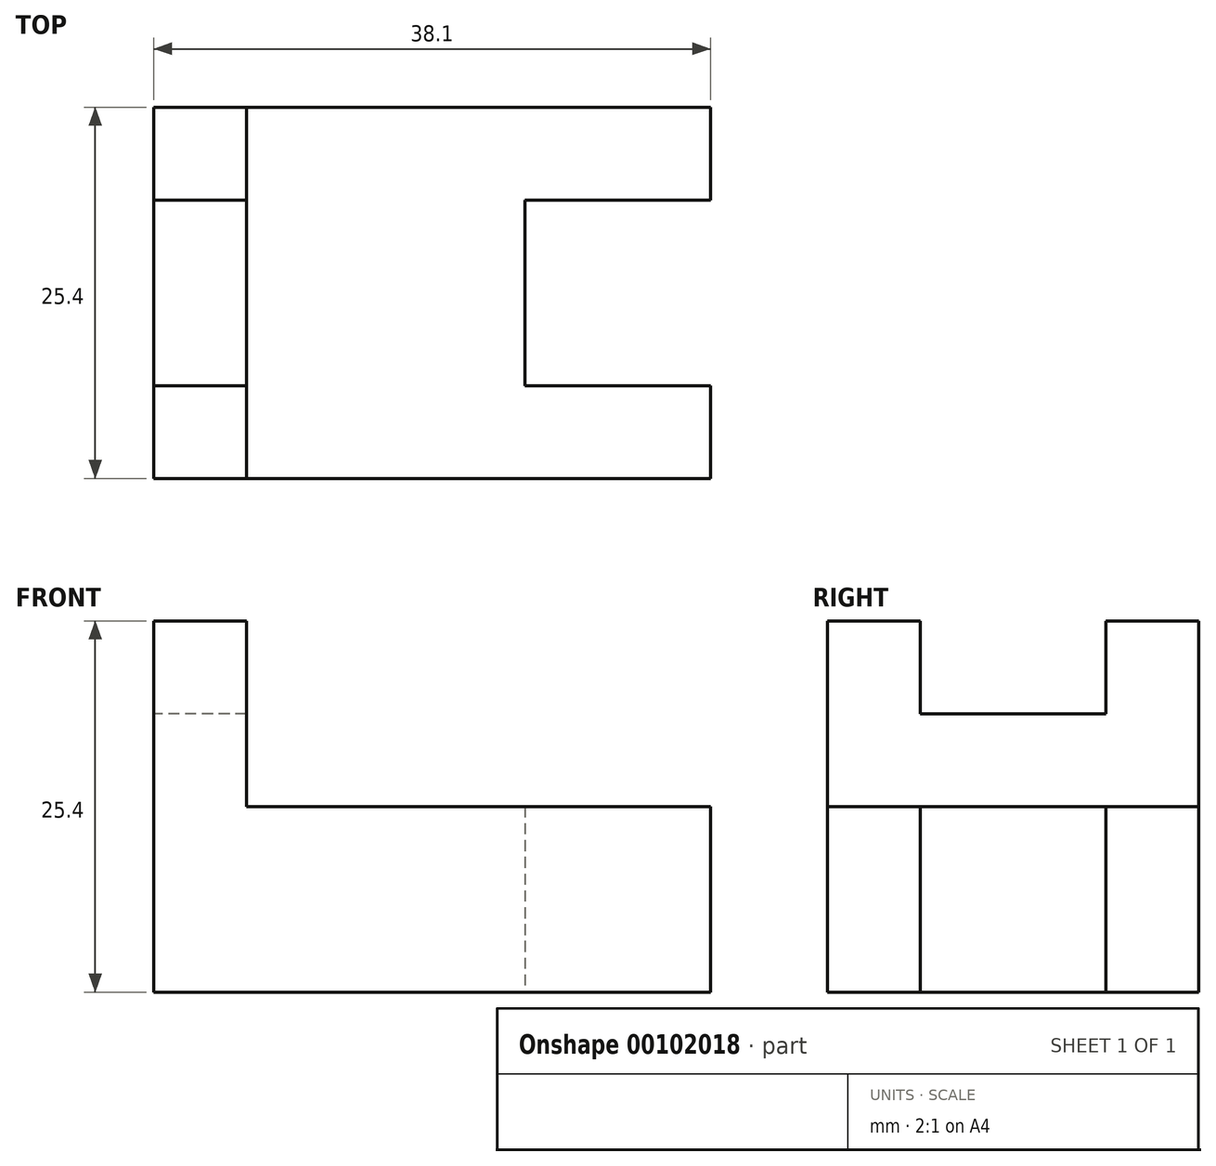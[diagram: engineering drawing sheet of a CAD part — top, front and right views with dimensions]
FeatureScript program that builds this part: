
annotation { "Feature Type Name" : "Feature", "Feature Type Description" : "" }
export const myFeature = defineFeature(function(context is Context, id is Id, definition is map)
    precondition{}
    {
        {
            var Q0;
            Q0=qCreatedBy(makeId("Top.planeOp"),FACE);
            var sketch = newSketch(context, id + "F0", { "sketchPlane" : qUnion([Q0])});
            skLineSegment(sketch, "E0", {"start": v(0, 0) * mm, "end": v(38.1, 0) * mm});
            skLineSegment(sketch, "E1", {"start": v(38.1, 0) * mm, "end": v(38.1, 6.35) * mm});
            skLineSegment(sketch, "E2", {"start": v(38.1, 6.35) * mm, "end": v(25.4, 6.35) * mm});
            skLineSegment(sketch, "E3", {"start": v(25.4, 6.35) * mm, "end": v(25.4, 19.05) * mm});
            skLineSegment(sketch, "E4", {"start": v(25.4, 19.05) * mm, "end": v(38.1, 19.05) * mm});
            skLineSegment(sketch, "E5", {"start": v(38.1, 19.05) * mm, "end": v(38.1, 25.4) * mm});
            skLineSegment(sketch, "E6", {"start": v(38.1, 25.4) * mm, "end": v(0, 25.4) * mm});
            skLineSegment(sketch, "E7", {"start": v(0, 25.4) * mm, "end": v(0, 0) * mm});
            skSolve(sketch);
        }
        {
            var Q0;
            Q0 = qSketchRegion(id + "F0", true);
            extrude(context, id + "F1", {"entities" : qUnion([Q0]), "depth" : 12.7 * mm});
        }
        {
            var Q0;
            Q0=makeQuery(id+"F1.opExtrude","CAP_FACE",FACE,{"disambiguationData":[OSD([sQuery(id+"F0.wireOp",EDGE,"E0"),sQuery(id+"F0.wireOp",EDGE,"E1"),sQuery(id+"F0.wireOp",EDGE,"E2"),sQuery(id+"F0.wireOp",EDGE,"E3"),sQuery(id+"F0.wireOp",EDGE,"E4"),sQuery(id+"F0.wireOp",EDGE,"E5"),sQuery(id+"F0.wireOp",EDGE,"E6"),sQuery(id+"F0.wireOp",EDGE,"E7")])],"isStart":false});
            var sketch = newSketch(context, id + "F2", { "sketchPlane" : qUnion([Q0])});
            skLineSegment(sketch, "E8", {"start": v(0, 0) * mm, "end": v(0, 25.4) * mm});
            skLineSegment(sketch, "E9", {"start": v(0, 25.4) * mm, "end": v(6.35, 25.4) * mm});
            skLineSegment(sketch, "E10", {"start": v(6.35, 25.4) * mm, "end": v(6.35, 0) * mm});
            skLineSegment(sketch, "E11", {"start": v(6.35, 0) * mm, "end": v(0, 0) * mm});
            skSolve(sketch);
        }
        {
            var Q0;
            Q0 = qSketchRegion(id + "F2", true);
            extrude(context, id + "F3", {"entities" : qUnion([Q0]), "operationType" : NewBodyOperationType.ADD, "depth" : 12.7 * mm});
        }
        {
            var Q0;
            Q0=makeQuery(id+"F3.opExtrude","CAP_FACE",FACE,{"disambiguationData":[OSD([sQuery(id+"F2.wireOp",EDGE,"E8"),sQuery(id+"F2.wireOp",EDGE,"E9"),sQuery(id+"F2.wireOp",EDGE,"E10"),sQuery(id+"F2.wireOp",EDGE,"E11")])],"isStart":false});
            var sketch = newSketch(context, id + "F4", { "sketchPlane" : qUnion([Q0])});
            skLineSegment(sketch, "E12.bottom", {"start": v(6.35, 19.05) * mm, "end": v(0, 19.05) * mm});
            skLineSegment(sketch, "E12.top", {"start": v(6.35, 6.35) * mm, "end": v(0, 6.35) * mm});
            skLineSegment(sketch, "E12.left", {"start": v(6.35, 19.05) * mm, "end": v(6.35, 6.35) * mm});
            skLineSegment(sketch, "E12.right", {"start": v(0, 19.05) * mm, "end": v(0, 6.35) * mm});
            skPoint(sketch, "E12.middle", {"position": v(3.17, 12.7) * mm});
            skPoint(sketch, "E12.middle.positionSnap0", {"position": v(3.17, 25.4) * mm});
            skPoint(sketch, "E12.middle.positionSnap1", {"position": v(6.35, 12.7) * mm});
            skPoint(sketch, "E12.centerSnap0", {"position": v(3.17, 25.4) * mm});
            skPoint(sketch, "E12.centerSnap1", {"position": v(6.35, 12.7) * mm});
            skSolve(sketch);
        }
        {
            var Q0;
            Q0=makeQuery(id+"F4.imprint","IMPRINT",FACE,{"disambiguationData":[TD([[makeQuery(id+"F4.imprint","IMPRINT",EDGE,{"derivedFrom":sQuery(id+"F4.wireOp",EDGE,"E12.bottom")}),1.0]])]});
            extrude(context, id + "F5", {"entities" : qUnion([Q0]), "operationType" : NewBodyOperationType.REMOVE, "oppositeDirection" : true, "depth" : 6.35 * mm});
        }
    });
